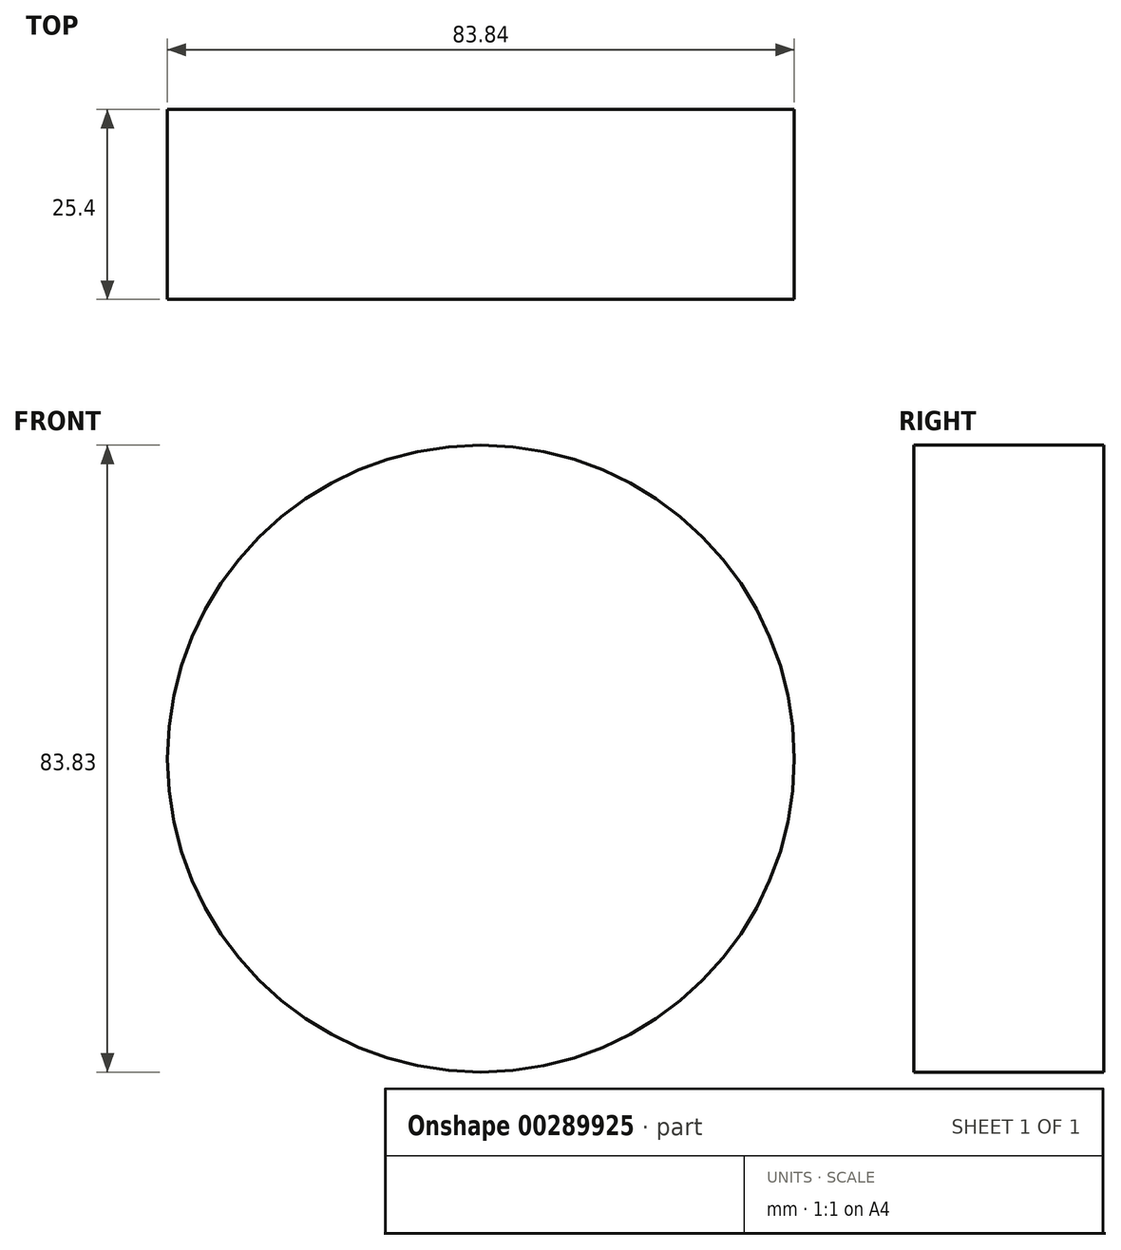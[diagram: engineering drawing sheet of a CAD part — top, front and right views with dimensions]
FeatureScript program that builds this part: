
annotation { "Feature Type Name" : "Feature", "Feature Type Description" : "" }
export const myFeature = defineFeature(function(context is Context, id is Id, definition is map)
    precondition{}
    {
        {
            var Q0;
            Q0=qCreatedBy(makeId("Front.planeOp"),FACE);
            var sketch = newSketch(context, id + "F0", { "sketchPlane" : qUnion([Q0])});
            skCircle(sketch, "E0", {"center": v(-23.4, 17.08) * mm, "radius": 41.92 * mm});
            skSolve(sketch);
        }
        {
            var Q0;
            Q0 = qSketchRegion(id + "F0", true);
            extrude(context, id + "F1", {"entities" : qUnion([Q0]), "depth" : 25.4 * mm});
        }
    });
